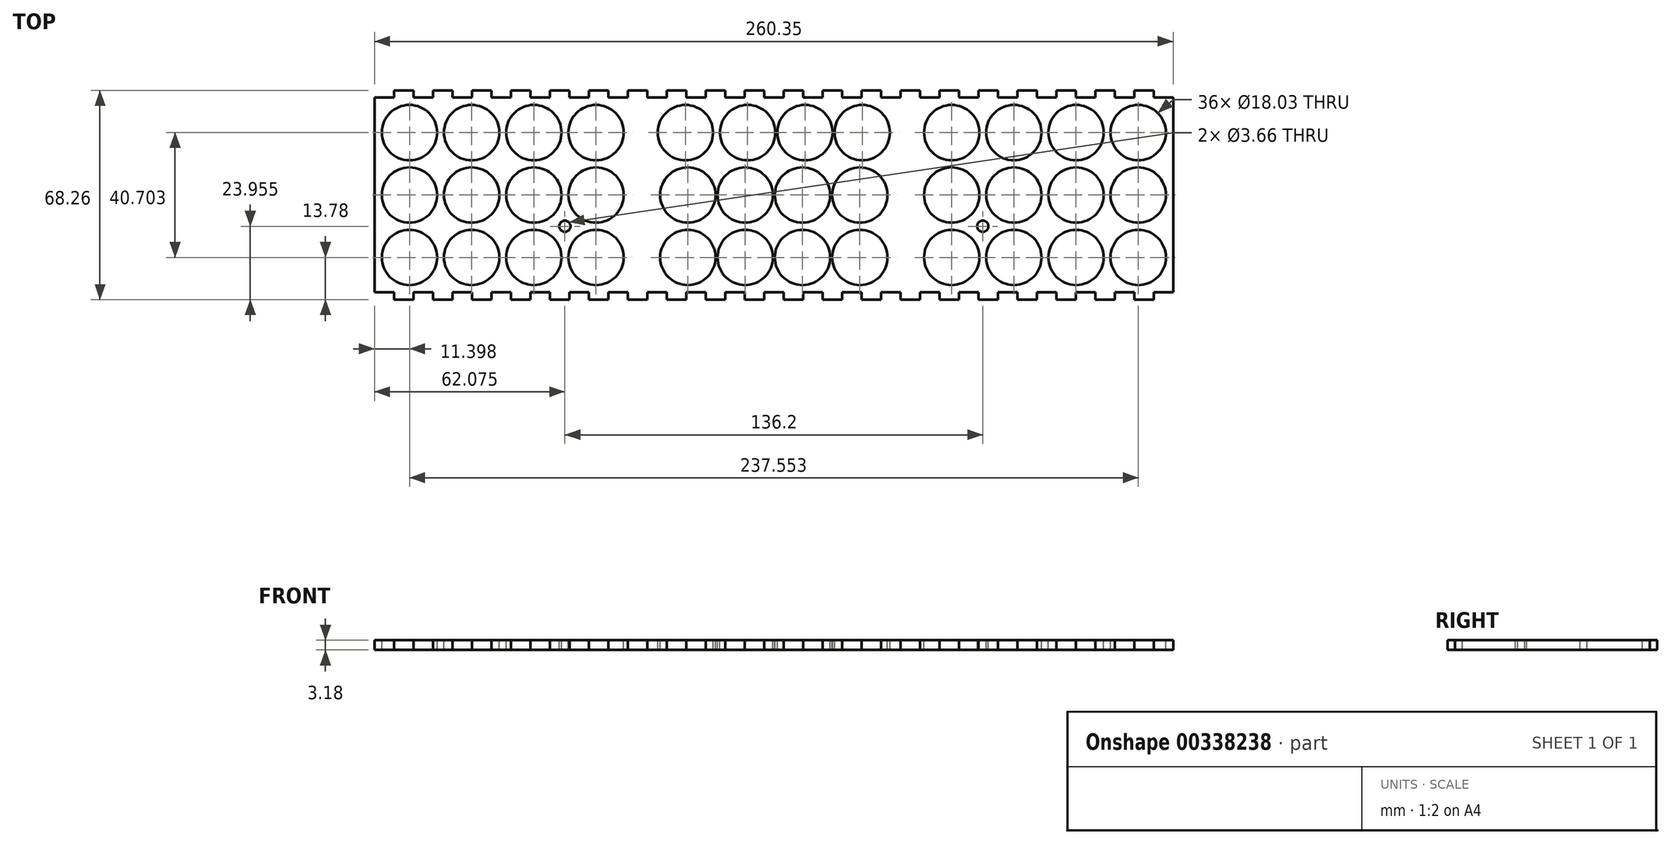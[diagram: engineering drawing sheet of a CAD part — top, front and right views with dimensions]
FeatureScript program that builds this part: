
annotation { "Feature Type Name" : "Feature", "Feature Type Description" : "" }
export const myFeature = defineFeature(function(context is Context, id is Id, definition is map)
    precondition{}
    {
        {
            var Q0;
            Q0=qCreatedBy(makeId("Top.planeOp"),FACE);
            var sketch = newSketch(context, id + "F0", { "sketchPlane" : qUnion([Q0])});
            skLineSegment(sketch, "E0.bottom", {"start": v(0, 0) * mm, "end": v(260.35, 0) * mm});
            skLineSegment(sketch, "E0.top", {"start": v(0, 68.26) * mm, "end": v(260.35, 68.26) * mm});
            skLineSegment(sketch, "E0.left", {"start": v(0, 0) * mm, "end": v(0, 68.26) * mm});
            skLineSegment(sketch, "E0.right", {"start": v(260.35, 0) * mm, "end": v(260.35, 68.26) * mm});
            skSolve(sketch);
        }
        {
            var Q0;
            Q0 = qSketchRegion(id + "F0", true);
            extrude(context, id + "F1", {"entities" : qUnion([Q0]), "depth" : 3.17 * mm});
        }
        {
            var Q0;
            Q0=makeQuery(id+"F1.opExtrude","CAP_FACE",FACE,{"disambiguationData":[OSD([sQuery(id+"F0.wireOp",EDGE,"E0.bottom"),sQuery(id+"F0.wireOp",EDGE,"E0.top"),sQuery(id+"F0.wireOp",EDGE,"E0.left"),sQuery(id+"F0.wireOp",EDGE,"E0.right")])],"isStart":false});
            var sketch = newSketch(context, id + "F2", { "sketchPlane" : qUnion([Q0])});
            skLineSegment(sketch, "E1.bottom", {"start": v(0, 0) * mm, "end": v(6.35, 0) * mm});
            skLineSegment(sketch, "E1.top", {"start": v(0, 2.38) * mm, "end": v(6.35, 2.38) * mm});
            skLineSegment(sketch, "E1.left", {"start": v(0, 0) * mm, "end": v(0, 2.38) * mm});
            skLineSegment(sketch, "E1.right", {"start": v(6.35, 0) * mm, "end": v(6.35, 2.38) * mm});
            skLineSegment(sketch, "E2", {"start": v(-2.38, 34.13) * mm, "end": v(0, 34.13) * mm, "construction": true});
            skLineSegment(sketch, "E3.MirrorCS", {"start": v(6.35, 68.26) * mm, "end": v(6.35, 65.88) * mm});
            skLineSegment(sketch, "E4.MirrorCS", {"start": v(0, 65.88) * mm, "end": v(6.35, 65.88) * mm});
            skLineSegment(sketch, "E5.MirrorCS", {"start": v(0, 68.26) * mm, "end": v(6.35, 68.26) * mm});
            skLineSegment(sketch, "E6.MirrorCS", {"start": v(0, 68.26) * mm, "end": v(0, 65.88) * mm});
            skCircle(sketch, "E7", {"center": v(11.4, 54.48) * mm, "radius": 9.02 * mm});
            skLineSegment(sketch, "E8", {"start": v(11.4, 54.48) * mm, "end": v(31.67, 54.48) * mm, "construction": true});
            skCircle(sketch, "E9", {"center": v(31.67, 54.48) * mm, "radius": 9.02 * mm});
            skLineSegment(sketch, "E10.1.0.0", {"start": v(31.67, 54.48) * mm, "end": v(51.94, 54.48) * mm, "construction": true});
            skCircle(sketch, "E10.1.0.1", {"center": v(51.94, 54.48) * mm, "radius": 9.02 * mm});
            skCircle(sketch, "E10.2.0.1", {"center": v(72.21, 54.48) * mm, "radius": 9.02 * mm});
            skLineSegment(sketch, "E11", {"start": v(0, 68.26) * mm, "end": v(0, 155.05) * mm, "construction": true});
            skLineSegment(sketch, "E12", {"start": v(0, 155.05) * mm, "end": v(86.78, 155.05) * mm, "construction": true});
            skLineSegment(sketch, "E13", {"start": v(86.78, 155.05) * mm, "end": v(173.57, 155.05) * mm, "construction": true});
            skLineSegment(sketch, "E14", {"start": v(173.57, 155.05) * mm, "end": v(260.35, 155.05) * mm, "construction": true});
            skLineSegment(sketch, "E15", {"start": v(260.35, 155.05) * mm, "end": v(260.35, 68.26) * mm, "construction": true});
            skLineSegment(sketch, "E16", {"start": v(86.78, 155.05) * mm, "end": v(86.78, 54.48) * mm, "construction": true});
            skLineSegment(sketch, "E17", {"start": v(0, 34.13) * mm, "end": v(2.38, 34.13) * mm, "construction": true});
            skCircle(sketch, "E18", {"center": v(101.36, 54.48) * mm, "radius": 9.02 * mm});
            skLineSegment(sketch, "E19", {"start": v(72.21, 54.48) * mm, "end": v(81.23, 54.48) * mm, "construction": true});
            skLineSegment(sketch, "E20", {"start": v(81.23, 54.48) * mm, "end": v(92.34, 54.48) * mm, "construction": true});
            skLineSegment(sketch, "E21", {"start": v(92.34, 54.48) * mm, "end": v(101.36, 54.48) * mm, "construction": true});
            skLineSegment(sketch, "E22", {"start": v(72.21, 54.48) * mm, "end": v(63.2, 54.48) * mm, "construction": true});
            skLineSegment(sketch, "E23", {"start": v(63.2, 54.48) * mm, "end": v(60.96, 54.48) * mm, "construction": true});
            skLineSegment(sketch, "E24", {"start": v(60.96, 54.48) * mm, "end": v(51.94, 54.48) * mm, "construction": true});
            skLineSegment(sketch, "E25", {"start": v(11.4, 54.48) * mm, "end": v(11.4, 63.5) * mm, "construction": true});
            skLineSegment(sketch, "E26", {"start": v(11.4, 54.48) * mm, "end": v(2.38, 54.48) * mm, "construction": true});
            skLineSegment(sketch, "E27", {"start": v(2.38, 54.48) * mm, "end": v(0, 54.48) * mm, "construction": true});
            skLineSegment(sketch, "E28", {"start": v(51.94, 54.48) * mm, "end": v(51.94, 34.21) * mm, "construction": true});
            skLineSegment(sketch, "E29", {"start": v(51.94, 34.21) * mm, "end": v(72.21, 34.21) * mm, "construction": true});
            skLineSegment(sketch, "E30", {"start": v(72.21, 34.21) * mm, "end": v(72.21, 54.48) * mm, "construction": true});
            skLineSegment(sketch, "E31", {"start": v(2.38, 34.13) * mm, "end": v(11.4, 34.13) * mm, "construction": true});
            skLineSegment(sketch, "E32", {"start": v(173.57, 155.05) * mm, "end": v(173.57, 54.48) * mm});
            skLineSegment(sketch, "E33", {"start": v(168.01, 54.48) * mm, "end": v(179.12, 54.48) * mm, "construction": true});
            skLineSegment(sketch, "E34", {"start": v(101.36, 54.48) * mm, "end": v(121.63, 54.48) * mm, "construction": true});
            skCircle(sketch, "E35", {"center": v(121.63, 54.48) * mm, "radius": 9.02 * mm});
            skCircle(sketch, "E36.1.0.0", {"center": v(140.31, 54.48) * mm, "radius": 9.02 * mm});
            skLineSegment(sketch, "E36.1.0.1", {"start": v(121.63, 54.48) * mm, "end": v(140.31, 54.48) * mm, "construction": true});
            skCircle(sketch, "E36.2.0.0", {"center": v(159, 54.48) * mm, "radius": 9.02 * mm});
            skLineSegment(sketch, "E36.2.0.1", {"start": v(140.31, 54.48) * mm, "end": v(159, 54.48) * mm, "construction": true});
            skLineSegment(sketch, "E37", {"start": v(159, 54.48) * mm, "end": v(168.01, 54.48) * mm, "construction": true});
            skLineSegment(sketch, "E38", {"start": v(179.12, 54.48) * mm, "end": v(188.14, 54.48) * mm, "construction": true});
            skCircle(sketch, "E39", {"center": v(188.14, 54.48) * mm, "radius": 9.02 * mm});
            skLineSegment(sketch, "E40", {"start": v(188.14, 54.48) * mm, "end": v(208.41, 54.48) * mm, "construction": true});
            skLineSegment(sketch, "E41", {"start": v(208.41, 54.48) * mm, "end": v(228.68, 54.48) * mm, "construction": true});
            skLineSegment(sketch, "E42", {"start": v(228.68, 54.48) * mm, "end": v(248.95, 54.48) * mm, "construction": true});
            skCircle(sketch, "E43", {"center": v(208.41, 54.48) * mm, "radius": 9.02 * mm});
            skCircle(sketch, "E44", {"center": v(228.68, 54.48) * mm, "radius": 9.02 * mm});
            skCircle(sketch, "E45", {"center": v(248.95, 54.48) * mm, "radius": 9.02 * mm});
            skCircle(sketch, "E46", {"center": v(11.4, 34.13) * mm, "radius": 9.02 * mm});
            skLineSegment(sketch, "E47", {"start": v(11.4, 34.13) * mm, "end": v(31.67, 34.13) * mm, "construction": true});
            skLineSegment(sketch, "E48", {"start": v(31.67, 34.13) * mm, "end": v(51.94, 34.13) * mm, "construction": true});
            skLineSegment(sketch, "E49", {"start": v(51.94, 34.13) * mm, "end": v(72.21, 34.13) * mm, "construction": true});
            skCircle(sketch, "E50", {"center": v(31.67, 34.13) * mm, "radius": 9.02 * mm});
            skCircle(sketch, "E51", {"center": v(51.94, 34.13) * mm, "radius": 9.02 * mm});
            skCircle(sketch, "E52", {"center": v(72.21, 34.13) * mm, "radius": 9.02 * mm});
            skLineSegment(sketch, "E53", {"start": v(260.35, 34.13) * mm, "end": v(257.97, 34.13) * mm, "construction": true});
            skLineSegment(sketch, "E54", {"start": v(257.97, 34.13) * mm, "end": v(248.95, 34.13) * mm, "construction": true});
            skCircle(sketch, "E55", {"center": v(248.95, 34.13) * mm, "radius": 9.02 * mm});
            skLineSegment(sketch, "E56", {"start": v(248.95, 34.13) * mm, "end": v(228.68, 34.13) * mm, "construction": true});
            skLineSegment(sketch, "E57", {"start": v(228.68, 34.13) * mm, "end": v(208.41, 34.13) * mm, "construction": true});
            skLineSegment(sketch, "E58", {"start": v(208.41, 34.13) * mm, "end": v(188.14, 34.13) * mm, "construction": true});
            skCircle(sketch, "E59", {"center": v(228.68, 34.13) * mm, "radius": 9.02 * mm});
            skCircle(sketch, "E60", {"center": v(208.41, 34.13) * mm, "radius": 9.02 * mm});
            skCircle(sketch, "E61", {"center": v(188.14, 34.13) * mm, "radius": 9.02 * mm});
            skLineSegment(sketch, "E62", {"start": v(72.21, 34.13) * mm, "end": v(102.15, 34.13) * mm, "construction": true});
            skLineSegment(sketch, "E63", {"start": v(102.15, 34.13) * mm, "end": v(120.83, 34.13) * mm, "construction": true});
            skLineSegment(sketch, "E64", {"start": v(120.83, 34.13) * mm, "end": v(139.52, 34.13) * mm, "construction": true});
            skLineSegment(sketch, "E65", {"start": v(139.52, 34.13) * mm, "end": v(158.2, 34.13) * mm, "construction": true});
            skCircle(sketch, "E66", {"center": v(102.15, 34.13) * mm, "radius": 9.02 * mm});
            skCircle(sketch, "E67", {"center": v(120.83, 34.13) * mm, "radius": 9.02 * mm});
            skCircle(sketch, "E68", {"center": v(139.52, 34.13) * mm, "radius": 9.02 * mm});
            skCircle(sketch, "E69", {"center": v(158.2, 34.13) * mm, "radius": 9.02 * mm});
            skLineSegment(sketch, "E70", {"start": v(158.2, 34.13) * mm, "end": v(188.14, 34.13) * mm, "construction": true});
            skLineSegment(sketch, "E71", {"start": v(0, 13.78) * mm, "end": v(2.38, 13.78) * mm, "construction": true});
            skLineSegment(sketch, "E72", {"start": v(2.38, 13.78) * mm, "end": v(11.4, 13.78) * mm, "construction": true});
            skCircle(sketch, "E73", {"center": v(11.4, 13.78) * mm, "radius": 9.02 * mm});
            skLineSegment(sketch, "E74", {"start": v(11.4, 13.78) * mm, "end": v(11.4, 4.76) * mm, "construction": true});
            skLineSegment(sketch, "E75", {"start": v(11.4, 4.76) * mm, "end": v(11.4, 2.38) * mm, "construction": true});
            skLineSegment(sketch, "E76", {"start": v(260.35, 13.78) * mm, "end": v(257.97, 13.78) * mm, "construction": true});
            skLineSegment(sketch, "E77", {"start": v(257.97, 13.78) * mm, "end": v(248.95, 13.78) * mm, "construction": true});
            skLineSegment(sketch, "E78", {"start": v(248.95, 13.78) * mm, "end": v(248.95, 4.76) * mm, "construction": true});
            skLineSegment(sketch, "E79", {"start": v(248.95, 4.76) * mm, "end": v(248.95, 2.38) * mm, "construction": true});
            skCircle(sketch, "E80", {"center": v(248.95, 13.78) * mm, "radius": 9.02 * mm});
            skLineSegment(sketch, "E81", {"start": v(248.95, 13.78) * mm, "end": v(228.68, 13.78) * mm, "construction": true});
            skLineSegment(sketch, "E82", {"start": v(228.68, 13.78) * mm, "end": v(208.41, 13.78) * mm, "construction": true});
            skLineSegment(sketch, "E83", {"start": v(208.41, 13.78) * mm, "end": v(188.14, 13.78) * mm, "construction": true});
            skCircle(sketch, "E84", {"center": v(228.68, 13.78) * mm, "radius": 9.02 * mm});
            skCircle(sketch, "E85", {"center": v(208.41, 13.78) * mm, "radius": 9.02 * mm});
            skCircle(sketch, "E86", {"center": v(188.14, 13.78) * mm, "radius": 9.02 * mm});
            skLineSegment(sketch, "E87", {"start": v(11.4, 13.78) * mm, "end": v(31.67, 13.78) * mm, "construction": true});
            skLineSegment(sketch, "E88", {"start": v(31.67, 13.78) * mm, "end": v(51.94, 13.78) * mm, "construction": true});
            skLineSegment(sketch, "E89", {"start": v(51.94, 13.78) * mm, "end": v(72.21, 13.78) * mm, "construction": true});
            skCircle(sketch, "E90", {"center": v(31.67, 13.78) * mm, "radius": 9.02 * mm});
            skCircle(sketch, "E91", {"center": v(51.94, 13.78) * mm, "radius": 9.02 * mm});
            skCircle(sketch, "E92", {"center": v(72.21, 13.78) * mm, "radius": 9.02 * mm});
            skLineSegment(sketch, "E93", {"start": v(102.15, 13.78) * mm, "end": v(120.83, 13.78) * mm, "construction": true});
            skLineSegment(sketch, "E94", {"start": v(120.83, 13.78) * mm, "end": v(139.52, 13.78) * mm, "construction": true});
            skLineSegment(sketch, "E95", {"start": v(139.52, 13.78) * mm, "end": v(158.2, 13.78) * mm, "construction": true});
            skCircle(sketch, "E96", {"center": v(102.15, 13.78) * mm, "radius": 9.02 * mm});
            skCircle(sketch, "E97", {"center": v(120.83, 13.78) * mm, "radius": 9.02 * mm});
            skCircle(sketch, "E98", {"center": v(139.52, 13.78) * mm, "radius": 9.02 * mm});
            skCircle(sketch, "E99", {"center": v(158.2, 13.78) * mm, "radius": 9.02 * mm});
            skLineSegment(sketch, "E100", {"start": v(72.21, 13.78) * mm, "end": v(102.15, 13.78) * mm, "construction": true});
            skLineSegment(sketch, "E101", {"start": v(188.14, 13.78) * mm, "end": v(158.2, 13.78) * mm, "construction": true});
            skLineSegment(sketch, "E102", {"start": v(6.35, 65.88) * mm, "end": v(12.7, 65.88) * mm, "construction": true});
            skLineSegment(sketch, "E103.bottom", {"start": v(12.7, 65.88) * mm, "end": v(19.05, 65.88) * mm});
            skLineSegment(sketch, "E103.top", {"start": v(12.7, 68.26) * mm, "end": v(19.05, 68.26) * mm});
            skLineSegment(sketch, "E103.left", {"start": v(12.7, 65.88) * mm, "end": v(12.7, 68.26) * mm});
            skLineSegment(sketch, "E103.right", {"start": v(19.05, 65.88) * mm, "end": v(19.05, 68.26) * mm});
            skLineSegment(sketch, "E104", {"start": v(6.35, 2.38) * mm, "end": v(12.7, 2.38) * mm, "construction": true});
            skLineSegment(sketch, "E105.bottom", {"start": v(12.7, 2.38) * mm, "end": v(19.05, 2.38) * mm});
            skLineSegment(sketch, "E105.top", {"start": v(12.7, 0) * mm, "end": v(19.05, 0) * mm});
            skLineSegment(sketch, "E105.left", {"start": v(12.7, 2.38) * mm, "end": v(12.7, 0) * mm});
            skLineSegment(sketch, "E105.right", {"start": v(19.05, 2.38) * mm, "end": v(19.05, 0) * mm});
            skLineSegment(sketch, "E106.1.0.0", {"start": v(25.4, 2.38) * mm, "end": v(31.75, 2.38) * mm});
            skLineSegment(sketch, "E106.1.0.1", {"start": v(25.4, 0) * mm, "end": v(31.75, 0) * mm});
            skLineSegment(sketch, "E106.1.0.2", {"start": v(19.05, 2.38) * mm, "end": v(25.4, 2.38) * mm, "construction": true});
            skLineSegment(sketch, "E106.1.0.3", {"start": v(25.4, 2.38) * mm, "end": v(25.4, 0) * mm});
            skLineSegment(sketch, "E106.1.0.4", {"start": v(31.75, 2.38) * mm, "end": v(31.75, 0) * mm});
            skLineSegment(sketch, "E106.2.0.0", {"start": v(38.1, 2.38) * mm, "end": v(44.45, 2.38) * mm});
            skLineSegment(sketch, "E106.2.0.1", {"start": v(38.1, 0) * mm, "end": v(44.45, 0) * mm});
            skLineSegment(sketch, "E106.2.0.2", {"start": v(31.75, 2.38) * mm, "end": v(38.1, 2.38) * mm, "construction": true});
            skLineSegment(sketch, "E106.2.0.3", {"start": v(38.1, 2.38) * mm, "end": v(38.1, 0) * mm});
            skLineSegment(sketch, "E106.2.0.4", {"start": v(44.45, 2.38) * mm, "end": v(44.45, 0) * mm});
            skLineSegment(sketch, "E106.direction1", {"start": v(6.35, 2.38) * mm, "end": v(19.05, 2.38) * mm, "construction": true});
            skLineSegment(sketch, "E107.0.3.0", {"start": v(50.8, 2.38) * mm, "end": v(57.15, 2.38) * mm});
            skLineSegment(sketch, "E107.3.3.0", {"start": v(50.8, 0) * mm, "end": v(57.15, 0) * mm});
            skLineSegment(sketch, "E107.6.3.0", {"start": v(44.45, 2.38) * mm, "end": v(50.8, 2.38) * mm, "construction": true});
            skLineSegment(sketch, "E107.9.3.0", {"start": v(50.8, 2.38) * mm, "end": v(50.8, 0) * mm});
            skLineSegment(sketch, "E107.12.3.0", {"start": v(57.15, 2.38) * mm, "end": v(57.15, 0) * mm});
            skLineSegment(sketch, "E107.0.4.0", {"start": v(63.5, 2.38) * mm, "end": v(69.85, 2.38) * mm});
            skLineSegment(sketch, "E107.3.4.0", {"start": v(63.5, 0) * mm, "end": v(69.85, 0) * mm});
            skLineSegment(sketch, "E107.6.4.0", {"start": v(57.15, 2.38) * mm, "end": v(63.5, 2.38) * mm, "construction": true});
            skLineSegment(sketch, "E107.9.4.0", {"start": v(63.5, 2.38) * mm, "end": v(63.5, 0) * mm});
            skLineSegment(sketch, "E107.12.4.0", {"start": v(69.85, 2.38) * mm, "end": v(69.85, 0) * mm});
            skLineSegment(sketch, "E107.0.5.0", {"start": v(76.2, 2.38) * mm, "end": v(82.55, 2.38) * mm});
            skLineSegment(sketch, "E107.3.5.0", {"start": v(76.2, 0) * mm, "end": v(82.55, 0) * mm});
            skLineSegment(sketch, "E107.6.5.0", {"start": v(69.85, 2.38) * mm, "end": v(76.2, 2.38) * mm, "construction": true});
            skLineSegment(sketch, "E107.9.5.0", {"start": v(76.2, 2.38) * mm, "end": v(76.2, 0) * mm});
            skLineSegment(sketch, "E107.12.5.0", {"start": v(82.55, 2.38) * mm, "end": v(82.55, 0) * mm});
            skLineSegment(sketch, "E107.0.6.0", {"start": v(88.9, 2.38) * mm, "end": v(95.25, 2.38) * mm});
            skLineSegment(sketch, "E107.3.6.0", {"start": v(88.9, 0) * mm, "end": v(95.25, 0) * mm});
            skLineSegment(sketch, "E107.6.6.0", {"start": v(82.55, 2.38) * mm, "end": v(88.9, 2.38) * mm, "construction": true});
            skLineSegment(sketch, "E107.9.6.0", {"start": v(88.9, 2.38) * mm, "end": v(88.9, 0) * mm});
            skLineSegment(sketch, "E107.12.6.0", {"start": v(95.25, 2.38) * mm, "end": v(95.25, 0) * mm});
            skLineSegment(sketch, "E107.0.7.0", {"start": v(101.6, 2.38) * mm, "end": v(107.95, 2.38) * mm});
            skLineSegment(sketch, "E107.3.7.0", {"start": v(101.6, 0) * mm, "end": v(107.95, 0) * mm});
            skLineSegment(sketch, "E107.6.7.0", {"start": v(95.25, 2.38) * mm, "end": v(101.6, 2.38) * mm, "construction": true});
            skLineSegment(sketch, "E107.9.7.0", {"start": v(101.6, 2.38) * mm, "end": v(101.6, 0) * mm});
            skLineSegment(sketch, "E107.12.7.0", {"start": v(107.95, 2.38) * mm, "end": v(107.95, 0) * mm});
            skLineSegment(sketch, "E107.0.8.0", {"start": v(114.3, 2.38) * mm, "end": v(120.65, 2.38) * mm});
            skLineSegment(sketch, "E107.3.8.0", {"start": v(114.3, 0) * mm, "end": v(120.65, 0) * mm});
            skLineSegment(sketch, "E107.6.8.0", {"start": v(107.95, 2.38) * mm, "end": v(114.3, 2.38) * mm, "construction": true});
            skLineSegment(sketch, "E107.9.8.0", {"start": v(114.3, 2.38) * mm, "end": v(114.3, 0) * mm});
            skLineSegment(sketch, "E107.12.8.0", {"start": v(120.65, 2.38) * mm, "end": v(120.65, 0) * mm});
            skLineSegment(sketch, "E107.0.9.0", {"start": v(127, 2.38) * mm, "end": v(133.35, 2.38) * mm});
            skLineSegment(sketch, "E107.3.9.0", {"start": v(127, 0) * mm, "end": v(133.35, 0) * mm});
            skLineSegment(sketch, "E107.6.9.0", {"start": v(120.65, 2.38) * mm, "end": v(127, 2.38) * mm, "construction": true});
            skLineSegment(sketch, "E107.9.9.0", {"start": v(127, 2.38) * mm, "end": v(127, 0) * mm});
            skLineSegment(sketch, "E107.12.9.0", {"start": v(133.35, 2.38) * mm, "end": v(133.35, 0) * mm});
            skLineSegment(sketch, "E107.0.10.0", {"start": v(139.7, 2.38) * mm, "end": v(146.05, 2.38) * mm});
            skLineSegment(sketch, "E107.3.10.0", {"start": v(139.7, 0) * mm, "end": v(146.05, 0) * mm});
            skLineSegment(sketch, "E107.6.10.0", {"start": v(133.35, 2.38) * mm, "end": v(139.7, 2.38) * mm, "construction": true});
            skLineSegment(sketch, "E107.9.10.0", {"start": v(139.7, 2.38) * mm, "end": v(139.7, 0) * mm});
            skLineSegment(sketch, "E107.12.10.0", {"start": v(146.05, 2.38) * mm, "end": v(146.05, 0) * mm});
            skLineSegment(sketch, "E107.0.11.0", {"start": v(152.4, 2.38) * mm, "end": v(158.75, 2.38) * mm});
            skLineSegment(sketch, "E107.3.11.0", {"start": v(152.4, 0) * mm, "end": v(158.75, 0) * mm});
            skLineSegment(sketch, "E107.6.11.0", {"start": v(146.05, 2.38) * mm, "end": v(152.4, 2.38) * mm, "construction": true});
            skLineSegment(sketch, "E107.9.11.0", {"start": v(152.4, 2.38) * mm, "end": v(152.4, 0) * mm});
            skLineSegment(sketch, "E107.12.11.0", {"start": v(158.75, 2.38) * mm, "end": v(158.75, 0) * mm});
            skLineSegment(sketch, "E107.0.12.0", {"start": v(165.1, 2.38) * mm, "end": v(171.45, 2.38) * mm});
            skLineSegment(sketch, "E107.3.12.0", {"start": v(165.1, 0) * mm, "end": v(171.45, 0) * mm});
            skLineSegment(sketch, "E107.6.12.0", {"start": v(158.75, 2.38) * mm, "end": v(165.1, 2.38) * mm, "construction": true});
            skLineSegment(sketch, "E107.9.12.0", {"start": v(165.1, 2.38) * mm, "end": v(165.1, 0) * mm});
            skLineSegment(sketch, "E107.12.12.0", {"start": v(171.45, 2.38) * mm, "end": v(171.45, 0) * mm});
            skLineSegment(sketch, "E107.0.13.0", {"start": v(177.8, 2.38) * mm, "end": v(184.15, 2.38) * mm});
            skLineSegment(sketch, "E107.3.13.0", {"start": v(177.8, 0) * mm, "end": v(184.15, 0) * mm});
            skLineSegment(sketch, "E107.6.13.0", {"start": v(171.45, 2.38) * mm, "end": v(177.8, 2.38) * mm, "construction": true});
            skLineSegment(sketch, "E107.9.13.0", {"start": v(177.8, 2.38) * mm, "end": v(177.8, 0) * mm});
            skLineSegment(sketch, "E107.12.13.0", {"start": v(184.15, 2.38) * mm, "end": v(184.15, 0) * mm});
            skLineSegment(sketch, "E107.0.14.0", {"start": v(190.5, 2.38) * mm, "end": v(196.85, 2.38) * mm});
            skLineSegment(sketch, "E107.3.14.0", {"start": v(190.5, 0) * mm, "end": v(196.85, 0) * mm});
            skLineSegment(sketch, "E107.6.14.0", {"start": v(184.15, 2.38) * mm, "end": v(190.5, 2.38) * mm, "construction": true});
            skLineSegment(sketch, "E107.9.14.0", {"start": v(190.5, 2.38) * mm, "end": v(190.5, 0) * mm});
            skLineSegment(sketch, "E107.12.14.0", {"start": v(196.85, 2.38) * mm, "end": v(196.85, 0) * mm});
            skLineSegment(sketch, "E107.0.15.0", {"start": v(203.2, 2.38) * mm, "end": v(209.55, 2.38) * mm});
            skLineSegment(sketch, "E107.3.15.0", {"start": v(203.2, 0) * mm, "end": v(209.55, 0) * mm});
            skLineSegment(sketch, "E107.6.15.0", {"start": v(196.85, 2.38) * mm, "end": v(203.2, 2.38) * mm, "construction": true});
            skLineSegment(sketch, "E107.9.15.0", {"start": v(203.2, 2.38) * mm, "end": v(203.2, 0) * mm});
            skLineSegment(sketch, "E107.12.15.0", {"start": v(209.55, 2.38) * mm, "end": v(209.55, 0) * mm});
            skLineSegment(sketch, "E107.0.16.0", {"start": v(215.9, 2.38) * mm, "end": v(222.25, 2.38) * mm});
            skLineSegment(sketch, "E107.3.16.0", {"start": v(215.9, 0) * mm, "end": v(222.25, 0) * mm});
            skLineSegment(sketch, "E107.6.16.0", {"start": v(209.55, 2.38) * mm, "end": v(215.9, 2.38) * mm, "construction": true});
            skLineSegment(sketch, "E107.9.16.0", {"start": v(215.9, 2.38) * mm, "end": v(215.9, 0) * mm});
            skLineSegment(sketch, "E107.12.16.0", {"start": v(222.25, 2.38) * mm, "end": v(222.25, 0) * mm});
            skLineSegment(sketch, "E107.0.17.0", {"start": v(228.6, 2.38) * mm, "end": v(234.95, 2.38) * mm});
            skLineSegment(sketch, "E107.3.17.0", {"start": v(228.6, 0) * mm, "end": v(234.95, 0) * mm});
            skLineSegment(sketch, "E107.6.17.0", {"start": v(222.25, 2.38) * mm, "end": v(228.6, 2.38) * mm, "construction": true});
            skLineSegment(sketch, "E107.9.17.0", {"start": v(228.6, 2.38) * mm, "end": v(228.6, 0) * mm});
            skLineSegment(sketch, "E107.12.17.0", {"start": v(234.95, 2.38) * mm, "end": v(234.95, 0) * mm});
            skLineSegment(sketch, "E107.0.18.0", {"start": v(241.3, 2.38) * mm, "end": v(247.65, 2.38) * mm});
            skLineSegment(sketch, "E107.3.18.0", {"start": v(241.3, 0) * mm, "end": v(247.65, 0) * mm});
            skLineSegment(sketch, "E107.6.18.0", {"start": v(234.95, 2.38) * mm, "end": v(241.3, 2.38) * mm, "construction": true});
            skLineSegment(sketch, "E107.9.18.0", {"start": v(241.3, 2.38) * mm, "end": v(241.3, 0) * mm});
            skLineSegment(sketch, "E107.12.18.0", {"start": v(247.65, 2.38) * mm, "end": v(247.65, 0) * mm});
            skLineSegment(sketch, "E107.0.19.0", {"start": v(254, 2.38) * mm, "end": v(260.35, 2.38) * mm});
            skLineSegment(sketch, "E107.3.19.0", {"start": v(254, 0) * mm, "end": v(260.35, 0) * mm});
            skLineSegment(sketch, "E107.6.19.0", {"start": v(247.65, 2.38) * mm, "end": v(254, 2.38) * mm, "construction": true});
            skLineSegment(sketch, "E107.9.19.0", {"start": v(254, 2.38) * mm, "end": v(254, 0) * mm});
            skLineSegment(sketch, "E107.12.19.0", {"start": v(260.35, 2.38) * mm, "end": v(260.35, 0) * mm});
            skLineSegment(sketch, "E107.0.20.0", {"start": v(266.7, 2.38) * mm, "end": v(273.05, 2.38) * mm});
            skLineSegment(sketch, "E107.3.20.0", {"start": v(266.7, 0) * mm, "end": v(273.05, 0) * mm});
            skLineSegment(sketch, "E107.6.20.0", {"start": v(260.35, 2.38) * mm, "end": v(266.7, 2.38) * mm, "construction": true});
            skLineSegment(sketch, "E107.9.20.0", {"start": v(266.7, 2.38) * mm, "end": v(266.7, 0) * mm});
            skLineSegment(sketch, "E107.12.20.0", {"start": v(273.05, 2.38) * mm, "end": v(273.05, 0) * mm});
            skLineSegment(sketch, "E107.0.21.0", {"start": v(279.4, 2.38) * mm, "end": v(285.75, 2.38) * mm});
            skLineSegment(sketch, "E107.3.21.0", {"start": v(279.4, 0) * mm, "end": v(285.75, 0) * mm});
            skLineSegment(sketch, "E107.6.21.0", {"start": v(273.05, 2.38) * mm, "end": v(279.4, 2.38) * mm, "construction": true});
            skLineSegment(sketch, "E107.9.21.0", {"start": v(279.4, 2.38) * mm, "end": v(279.4, 0) * mm});
            skLineSegment(sketch, "E107.12.21.0", {"start": v(285.75, 2.38) * mm, "end": v(285.75, 0) * mm});
            skLineSegment(sketch, "E108.1.0.0", {"start": v(25.4, 65.88) * mm, "end": v(31.75, 65.88) * mm});
            skLineSegment(sketch, "E108.1.0.1", {"start": v(25.4, 65.88) * mm, "end": v(25.4, 68.26) * mm});
            skLineSegment(sketch, "E108.1.0.2", {"start": v(25.4, 68.26) * mm, "end": v(31.75, 68.26) * mm});
            skLineSegment(sketch, "E108.1.0.3", {"start": v(31.75, 65.88) * mm, "end": v(31.75, 68.26) * mm});
            skLineSegment(sketch, "E108.1.0.4", {"start": v(19.05, 65.88) * mm, "end": v(25.4, 65.88) * mm, "construction": true});
            skLineSegment(sketch, "E108.2.0.0", {"start": v(38.1, 65.88) * mm, "end": v(44.45, 65.88) * mm});
            skLineSegment(sketch, "E108.2.0.1", {"start": v(38.1, 65.88) * mm, "end": v(38.1, 68.26) * mm});
            skLineSegment(sketch, "E108.2.0.2", {"start": v(38.1, 68.26) * mm, "end": v(44.45, 68.26) * mm});
            skLineSegment(sketch, "E108.2.0.3", {"start": v(44.45, 65.88) * mm, "end": v(44.45, 68.26) * mm});
            skLineSegment(sketch, "E108.2.0.4", {"start": v(31.75, 65.88) * mm, "end": v(38.1, 65.88) * mm, "construction": true});
            skLineSegment(sketch, "E108.3.0.0", {"start": v(50.8, 65.88) * mm, "end": v(57.15, 65.88) * mm});
            skLineSegment(sketch, "E108.3.0.1", {"start": v(50.8, 65.88) * mm, "end": v(50.8, 68.26) * mm});
            skLineSegment(sketch, "E108.3.0.2", {"start": v(50.8, 68.26) * mm, "end": v(57.15, 68.26) * mm});
            skLineSegment(sketch, "E108.3.0.3", {"start": v(57.15, 65.88) * mm, "end": v(57.15, 68.26) * mm});
            skLineSegment(sketch, "E108.3.0.4", {"start": v(44.45, 65.88) * mm, "end": v(50.8, 65.88) * mm, "construction": true});
            skLineSegment(sketch, "E108.4.0.0", {"start": v(63.5, 65.88) * mm, "end": v(69.85, 65.88) * mm});
            skLineSegment(sketch, "E108.4.0.1", {"start": v(63.5, 65.88) * mm, "end": v(63.5, 68.26) * mm});
            skLineSegment(sketch, "E108.4.0.2", {"start": v(63.5, 68.26) * mm, "end": v(69.85, 68.26) * mm});
            skLineSegment(sketch, "E108.4.0.3", {"start": v(69.85, 65.88) * mm, "end": v(69.85, 68.26) * mm});
            skLineSegment(sketch, "E108.4.0.4", {"start": v(57.15, 65.88) * mm, "end": v(63.5, 65.88) * mm, "construction": true});
            skLineSegment(sketch, "E108.5.0.0", {"start": v(76.2, 65.88) * mm, "end": v(82.55, 65.88) * mm});
            skLineSegment(sketch, "E108.5.0.1", {"start": v(76.2, 65.88) * mm, "end": v(76.2, 68.26) * mm});
            skLineSegment(sketch, "E108.5.0.2", {"start": v(76.2, 68.26) * mm, "end": v(82.55, 68.26) * mm});
            skLineSegment(sketch, "E108.5.0.3", {"start": v(82.55, 65.88) * mm, "end": v(82.55, 68.26) * mm});
            skLineSegment(sketch, "E108.5.0.4", {"start": v(69.85, 65.88) * mm, "end": v(76.2, 65.88) * mm, "construction": true});
            skLineSegment(sketch, "E108.6.0.0", {"start": v(88.9, 65.88) * mm, "end": v(95.25, 65.88) * mm});
            skLineSegment(sketch, "E108.6.0.1", {"start": v(88.9, 65.88) * mm, "end": v(88.9, 68.26) * mm});
            skLineSegment(sketch, "E108.6.0.2", {"start": v(88.9, 68.26) * mm, "end": v(95.25, 68.26) * mm});
            skLineSegment(sketch, "E108.6.0.3", {"start": v(95.25, 65.88) * mm, "end": v(95.25, 68.26) * mm});
            skLineSegment(sketch, "E108.6.0.4", {"start": v(82.55, 65.88) * mm, "end": v(88.9, 65.88) * mm, "construction": true});
            skLineSegment(sketch, "E108.7.0.0", {"start": v(101.6, 65.88) * mm, "end": v(107.95, 65.88) * mm});
            skLineSegment(sketch, "E108.7.0.1", {"start": v(101.6, 65.88) * mm, "end": v(101.6, 68.26) * mm});
            skLineSegment(sketch, "E108.7.0.2", {"start": v(101.6, 68.26) * mm, "end": v(107.95, 68.26) * mm});
            skLineSegment(sketch, "E108.7.0.3", {"start": v(107.95, 65.88) * mm, "end": v(107.95, 68.26) * mm});
            skLineSegment(sketch, "E108.7.0.4", {"start": v(95.25, 65.88) * mm, "end": v(101.6, 65.88) * mm, "construction": true});
            skLineSegment(sketch, "E108.8.0.0", {"start": v(114.3, 65.88) * mm, "end": v(120.65, 65.88) * mm});
            skLineSegment(sketch, "E108.8.0.1", {"start": v(114.3, 65.88) * mm, "end": v(114.3, 68.26) * mm});
            skLineSegment(sketch, "E108.8.0.2", {"start": v(114.3, 68.26) * mm, "end": v(120.65, 68.26) * mm});
            skLineSegment(sketch, "E108.8.0.3", {"start": v(120.65, 65.88) * mm, "end": v(120.65, 68.26) * mm});
            skLineSegment(sketch, "E108.8.0.4", {"start": v(107.95, 65.88) * mm, "end": v(114.3, 65.88) * mm, "construction": true});
            skLineSegment(sketch, "E108.9.0.0", {"start": v(127, 65.88) * mm, "end": v(133.35, 65.88) * mm});
            skLineSegment(sketch, "E108.9.0.1", {"start": v(127, 65.88) * mm, "end": v(127, 68.26) * mm});
            skLineSegment(sketch, "E108.9.0.2", {"start": v(127, 68.26) * mm, "end": v(133.35, 68.26) * mm});
            skLineSegment(sketch, "E108.9.0.3", {"start": v(133.35, 65.88) * mm, "end": v(133.35, 68.26) * mm});
            skLineSegment(sketch, "E108.9.0.4", {"start": v(120.65, 65.88) * mm, "end": v(127, 65.88) * mm, "construction": true});
            skLineSegment(sketch, "E108.10.0.0", {"start": v(139.7, 65.88) * mm, "end": v(146.05, 65.88) * mm});
            skLineSegment(sketch, "E108.10.0.1", {"start": v(139.7, 65.88) * mm, "end": v(139.7, 68.26) * mm});
            skLineSegment(sketch, "E108.10.0.2", {"start": v(139.7, 68.26) * mm, "end": v(146.05, 68.26) * mm});
            skLineSegment(sketch, "E108.10.0.3", {"start": v(146.05, 65.88) * mm, "end": v(146.05, 68.26) * mm});
            skLineSegment(sketch, "E108.10.0.4", {"start": v(133.35, 65.88) * mm, "end": v(139.7, 65.88) * mm, "construction": true});
            skLineSegment(sketch, "E108.11.0.0", {"start": v(152.4, 65.88) * mm, "end": v(158.75, 65.88) * mm});
            skLineSegment(sketch, "E108.11.0.1", {"start": v(152.4, 65.88) * mm, "end": v(152.4, 68.26) * mm});
            skLineSegment(sketch, "E108.11.0.2", {"start": v(152.4, 68.26) * mm, "end": v(158.75, 68.26) * mm});
            skLineSegment(sketch, "E108.11.0.3", {"start": v(158.75, 65.88) * mm, "end": v(158.75, 68.26) * mm});
            skLineSegment(sketch, "E108.11.0.4", {"start": v(146.05, 65.88) * mm, "end": v(152.4, 65.88) * mm, "construction": true});
            skLineSegment(sketch, "E108.12.0.0", {"start": v(165.1, 65.88) * mm, "end": v(171.45, 65.88) * mm});
            skLineSegment(sketch, "E108.12.0.1", {"start": v(165.1, 65.88) * mm, "end": v(165.1, 68.26) * mm});
            skLineSegment(sketch, "E108.12.0.2", {"start": v(165.1, 68.26) * mm, "end": v(171.45, 68.26) * mm});
            skLineSegment(sketch, "E108.12.0.3", {"start": v(171.45, 65.88) * mm, "end": v(171.45, 68.26) * mm});
            skLineSegment(sketch, "E108.12.0.4", {"start": v(158.75, 65.88) * mm, "end": v(165.1, 65.88) * mm, "construction": true});
            skLineSegment(sketch, "E108.13.0.0", {"start": v(177.8, 65.88) * mm, "end": v(184.15, 65.88) * mm});
            skLineSegment(sketch, "E108.13.0.1", {"start": v(177.8, 65.88) * mm, "end": v(177.8, 68.26) * mm});
            skLineSegment(sketch, "E108.13.0.2", {"start": v(177.8, 68.26) * mm, "end": v(184.15, 68.26) * mm});
            skLineSegment(sketch, "E108.13.0.3", {"start": v(184.15, 65.88) * mm, "end": v(184.15, 68.26) * mm});
            skLineSegment(sketch, "E108.13.0.4", {"start": v(171.45, 65.88) * mm, "end": v(177.8, 65.88) * mm, "construction": true});
            skLineSegment(sketch, "E108.14.0.0", {"start": v(190.5, 65.88) * mm, "end": v(196.85, 65.88) * mm});
            skLineSegment(sketch, "E108.14.0.1", {"start": v(190.5, 65.88) * mm, "end": v(190.5, 68.26) * mm});
            skLineSegment(sketch, "E108.14.0.2", {"start": v(190.5, 68.26) * mm, "end": v(196.85, 68.26) * mm});
            skLineSegment(sketch, "E108.14.0.3", {"start": v(196.85, 65.88) * mm, "end": v(196.85, 68.26) * mm});
            skLineSegment(sketch, "E108.14.0.4", {"start": v(184.15, 65.88) * mm, "end": v(190.5, 65.88) * mm, "construction": true});
            skLineSegment(sketch, "E108.15.0.0", {"start": v(203.2, 65.88) * mm, "end": v(209.55, 65.88) * mm});
            skLineSegment(sketch, "E108.15.0.1", {"start": v(203.2, 65.88) * mm, "end": v(203.2, 68.26) * mm});
            skLineSegment(sketch, "E108.15.0.2", {"start": v(203.2, 68.26) * mm, "end": v(209.55, 68.26) * mm});
            skLineSegment(sketch, "E108.15.0.3", {"start": v(209.55, 65.88) * mm, "end": v(209.55, 68.26) * mm});
            skLineSegment(sketch, "E108.15.0.4", {"start": v(196.85, 65.88) * mm, "end": v(203.2, 65.88) * mm, "construction": true});
            skLineSegment(sketch, "E108.16.0.0", {"start": v(215.9, 65.88) * mm, "end": v(222.25, 65.88) * mm});
            skLineSegment(sketch, "E108.16.0.1", {"start": v(215.9, 65.88) * mm, "end": v(215.9, 68.26) * mm});
            skLineSegment(sketch, "E108.16.0.2", {"start": v(215.9, 68.26) * mm, "end": v(222.25, 68.26) * mm});
            skLineSegment(sketch, "E108.16.0.3", {"start": v(222.25, 65.88) * mm, "end": v(222.25, 68.26) * mm});
            skLineSegment(sketch, "E108.16.0.4", {"start": v(209.55, 65.88) * mm, "end": v(215.9, 65.88) * mm, "construction": true});
            skLineSegment(sketch, "E108.17.0.0", {"start": v(228.6, 65.88) * mm, "end": v(234.95, 65.88) * mm});
            skLineSegment(sketch, "E108.17.0.1", {"start": v(228.6, 65.88) * mm, "end": v(228.6, 68.26) * mm});
            skLineSegment(sketch, "E108.17.0.2", {"start": v(228.6, 68.26) * mm, "end": v(234.95, 68.26) * mm});
            skLineSegment(sketch, "E108.17.0.3", {"start": v(234.95, 65.88) * mm, "end": v(234.95, 68.26) * mm});
            skLineSegment(sketch, "E108.17.0.4", {"start": v(222.25, 65.88) * mm, "end": v(228.6, 65.88) * mm, "construction": true});
            skLineSegment(sketch, "E108.18.0.0", {"start": v(241.3, 65.88) * mm, "end": v(247.65, 65.88) * mm});
            skLineSegment(sketch, "E108.18.0.1", {"start": v(241.3, 65.88) * mm, "end": v(241.3, 68.26) * mm});
            skLineSegment(sketch, "E108.18.0.2", {"start": v(241.3, 68.26) * mm, "end": v(247.65, 68.26) * mm});
            skLineSegment(sketch, "E108.18.0.3", {"start": v(247.65, 65.88) * mm, "end": v(247.65, 68.26) * mm});
            skLineSegment(sketch, "E108.18.0.4", {"start": v(234.95, 65.88) * mm, "end": v(241.3, 65.88) * mm, "construction": true});
            skLineSegment(sketch, "E108.19.0.0", {"start": v(254, 65.88) * mm, "end": v(260.35, 65.88) * mm});
            skLineSegment(sketch, "E108.19.0.1", {"start": v(254, 65.88) * mm, "end": v(254, 68.26) * mm});
            skLineSegment(sketch, "E108.19.0.2", {"start": v(254, 68.26) * mm, "end": v(260.35, 68.26) * mm});
            skLineSegment(sketch, "E108.19.0.3", {"start": v(260.35, 65.88) * mm, "end": v(260.35, 68.26) * mm});
            skLineSegment(sketch, "E108.19.0.4", {"start": v(247.65, 65.88) * mm, "end": v(254, 65.88) * mm, "construction": true});
            skLineSegment(sketch, "E108.20.0.0", {"start": v(266.7, 65.88) * mm, "end": v(273.05, 65.88) * mm});
            skLineSegment(sketch, "E108.20.0.1", {"start": v(266.7, 65.88) * mm, "end": v(266.7, 68.26) * mm});
            skLineSegment(sketch, "E108.20.0.2", {"start": v(266.7, 68.26) * mm, "end": v(273.05, 68.26) * mm});
            skLineSegment(sketch, "E108.20.0.3", {"start": v(273.05, 65.88) * mm, "end": v(273.05, 68.26) * mm});
            skLineSegment(sketch, "E108.20.0.4", {"start": v(260.35, 65.88) * mm, "end": v(266.7, 65.88) * mm, "construction": true});
            skLineSegment(sketch, "E108.21.0.0", {"start": v(279.4, 65.88) * mm, "end": v(285.75, 65.88) * mm});
            skLineSegment(sketch, "E108.21.0.1", {"start": v(279.4, 65.88) * mm, "end": v(279.4, 68.26) * mm});
            skLineSegment(sketch, "E108.21.0.2", {"start": v(279.4, 68.26) * mm, "end": v(285.75, 68.26) * mm});
            skLineSegment(sketch, "E108.21.0.3", {"start": v(285.75, 65.88) * mm, "end": v(285.75, 68.26) * mm});
            skLineSegment(sketch, "E108.21.0.4", {"start": v(273.05, 65.88) * mm, "end": v(279.4, 65.88) * mm, "construction": true});
            skLineSegment(sketch, "E108.direction1", {"start": v(6.35, 65.88) * mm, "end": v(19.05, 65.88) * mm, "construction": true});
            skLineSegment(sketch, "E109", {"start": v(11.4, 63.5) * mm, "end": v(11.4, 65.88) * mm, "construction": true});
            skCircle(sketch, "E110", {"center": v(62.07, 23.96) * mm, "radius": 5.35 * mm, "construction": true});
            skCircle(sketch, "E111", {"center": v(62.07, 23.96) * mm, "radius": 1.83 * mm});
            skCircle(sketch, "E112", {"center": v(198.28, 23.96) * mm, "radius": 5.35 * mm, "construction": true});
            skCircle(sketch, "E113", {"center": v(198.28, 23.96) * mm, "radius": 1.83 * mm});
            skSolve(sketch);
        }
        {
            var Q0;
            Q0 = qSketchRegion(id + "F2", true);
            var Q1;
            Q1=makeQuery(id+"F1.opExtrude","CAP_FACE",FACE,{"disambiguationData":[OSD([sQuery(id+"F0.wireOp",EDGE,"E0.bottom"),sQuery(id+"F0.wireOp",EDGE,"E0.top"),sQuery(id+"F0.wireOp",EDGE,"E0.left"),sQuery(id+"F0.wireOp",EDGE,"E0.right")])],"isStart":true});
            extrude(context, id + "F3", {"entities" : qUnion([Q0]), "operationType" : NewBodyOperationType.REMOVE, "endBound" : BoundingType.UP_TO_SURFACE, "oppositeDirection" : true, "endBoundEntityFace" : qUnion([Q1]), "depth" : 25.4 * mm});
        }
    });
